# Revit family: Furniture_Tables_Svedholm_Cylinder
name_source: partatom
category: Furniture
revit_build: Autodesk Revit 2018 (Build: 20190510_1515(x64)
units: mm (PartAtom-declared; Revit-internal decimal feet)

## family parameters
Always vertical = Yes
Cut with Voids When Loaded = No
OmniClass Number = 23.21.23.00
OmniClass Title = Residential Furniture and Equipment
Room Calculation Point = No
Shared = No
Work Plane-Based = Yes

## types (3) — shared parameters
BIMobject category = Tables
Default Elevation = 1219 mm
Description = A lounge and side table with table top of tempered glass with ceramic paint. Table base of chrome-plated alternatively powder coated steel tube.
Design country = Sweden
Detail material = Svedholm - Metal - RAL 9005 Jet black
Edition number = 1
IFC Classification = Furniture
Manufacturer = Svedholm
Manufacturer country = Sweden
Manufacturer name = Svedholm
Material main = Glass
Material secondary = Polished Chrome
Model = Cylinder
OmniClass Code = 23-21 23 00
OmniClass Description = Residential Furniture and Equipment
Product Guid = 1495e2cd-a1cf-4592-a12f-a3827c337f62
Product SKU = Cylinder
Product data url = https://bimobject.com
Product family = Cylinder
Product group = Tables
Product name = Cylinder
Product url = https://www.svedholm.se
QR code = https://bimobject.com
Secondary material = Svedholm - Glass - Transparent
UNSPSC Code = 56
URL = https://www.svedholm.se
Uniclass 1.4 Code = L8221
Uniclass 1.4 Description = Tables

## per-type parameters (varying)
| type | 450x600mm | 675x450mm | 900x300mm |
| ART - (306.600.001) Tabletop dim. - (450) Table height - (600) | Yes | No | No |
| ART - (306.600.002) Tabletop dim. - (675) Table height - (450) | No | Yes | No |
| ART - (306.600.003) Tabletop dim. - (900) Table height - (300) | No | No | Yes |

## geometry (parser evidence)
native form markers: Sweep x3
no freeform markers — native parametric forms only
